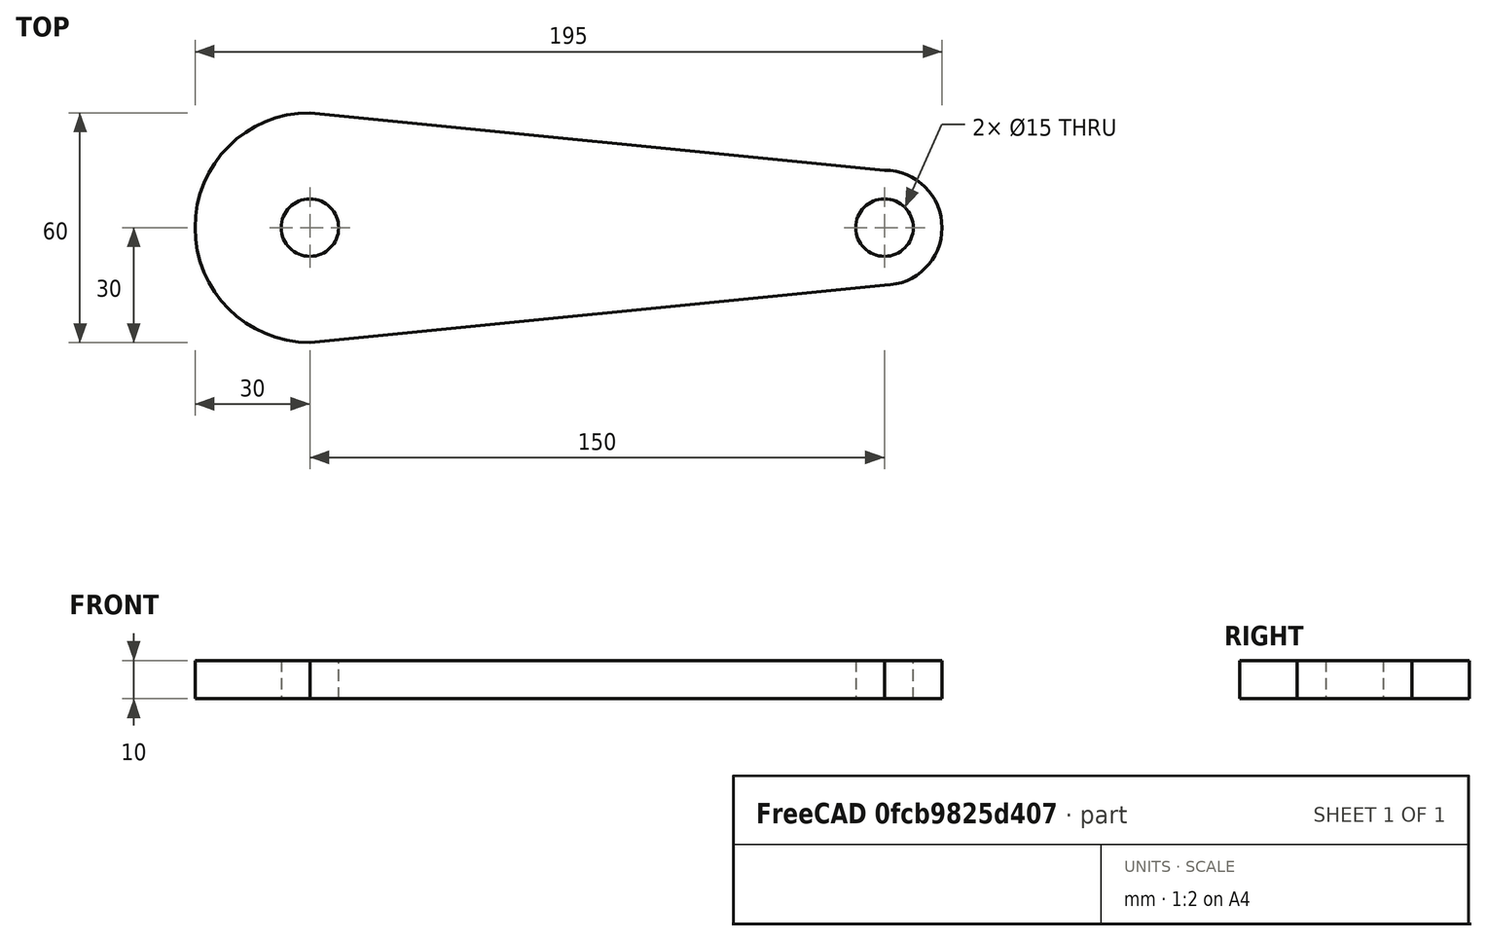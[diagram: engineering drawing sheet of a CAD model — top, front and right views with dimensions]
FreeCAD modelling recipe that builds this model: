
FCSTD DOCUMENT  (FreeCAD 0.18R4 (GitTag))
Label: foreArm
License: All rights reserved
LicenseURL: http://en.wikipedia.org/wiki/All_rights_reserved
objects: Sketcher::SketchObject×1, PartDesign::Pad×1, PartDesign::Body×1, App::Part×1, Part::Feature×1
note: 5 computed .brp shape members not serialized (recipe doc carries the construction recipe); baked Part::Feature solids carry a one-line shape summary decoded from their .brp

FEATURE [Sketcher::SketchObject] Sketch
  MapMode = 5
  Support = -> [XY_Plane001]
  sketch-geometry (6):
    g0: ArcOfCircle CenterX=150 CenterY=0 CenterZ=0 NormalX=0 NormalY=0 NormalZ=1 AngleXU=0 Radius=15 StartAngle=4.71239 EndAngle=7.85398
    g1: Circle CenterX=150 CenterY=0 CenterZ=0 NormalX=0 NormalY=0 NormalZ=1 AngleXU=0 Radius=7.5
    g2: LineSegment StartX=-2.76e-14 StartY=30 StartZ=0 EndX=150 EndY=15 EndZ=0
    g3: LineSegment StartX=-2.76e-14 StartY=-30 StartZ=0 EndX=150 EndY=-15 EndZ=0
    g4: ArcOfCircle CenterX=-2.76e-14 CenterY=0 CenterZ=0 NormalX=0 NormalY=0 NormalZ=1 AngleXU=0 Radius=30 StartAngle=1.5708 EndAngle=4.71239
    g5: Circle CenterX=-2.76e-14 CenterY=0 CenterZ=0 NormalX=0 NormalY=0 NormalZ=1 AngleXU=0 Radius=7.5
  constraints (17):
    c: Radius(g0) = 15
    c: Diameter(g1) = 15
    c: Coincident(g0,g1)
    c: Vertical(g2,g0)
    c: Vertical(g0,g3)
    c: Coincident(g0,g3)
    c: Coincident(g0,g2)
    c: Coincident(g4,g-1)
    c: Coincident(g4,g2)
    c: Vertical(g4,g2)
    c: Vertical(g2,g3)
    c: Coincident(g4,g3)
    c: Radius(g4) = 30
    c: DistanceX(g4,g0) = 150
    c: Horizontal(g4,g0)
    c: Diameter(g5) = 15
    c: Coincident(g5,g4)
FEATURE [PartDesign::Pad] Pad
  Length = 10
  Length2 = 100
  Profile = -> Sketch
  Type = 0
FEATURE [PartDesign::Body] Body  label="foreArm"
  Group = -> [Sketch,Pad]
  Origin = -> Origin001
  Tip = -> Pad
FEATURE [App::Part] Part
  Group = -> [Body]
  Origin = -> Origin
FEATURE [Part::Feature] Pad001  label="Robot_ForeArm"
  shape: bbox 195 x 60 x 10 mm, 8 faces (baked)
